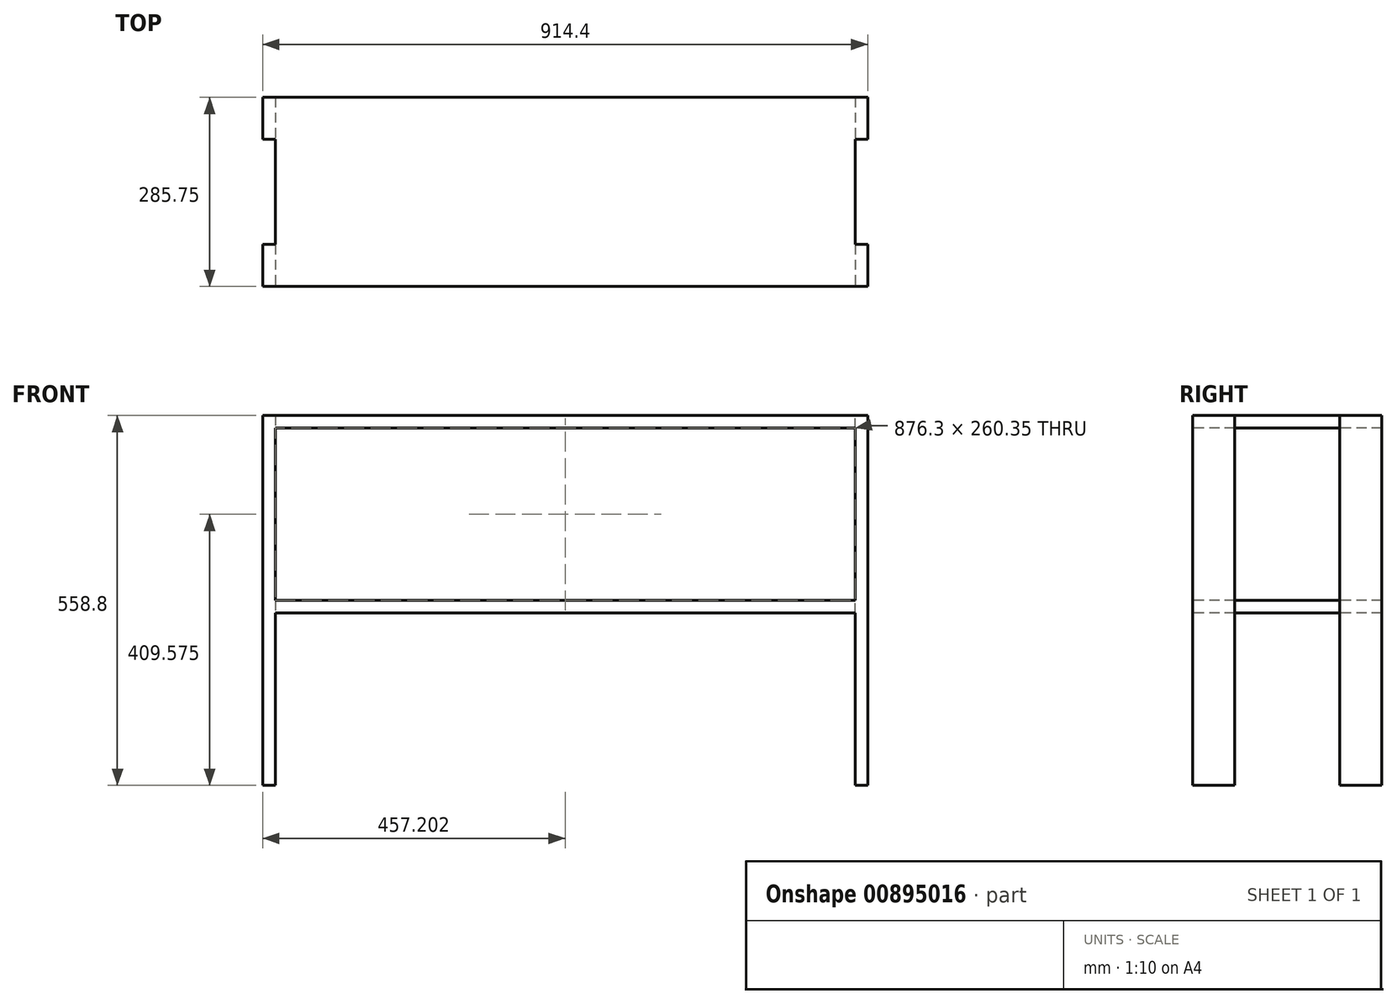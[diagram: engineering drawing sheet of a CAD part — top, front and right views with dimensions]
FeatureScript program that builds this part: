
annotation { "Feature Type Name" : "Feature", "Feature Type Description" : "" }
export const myFeature = defineFeature(function(context is Context, id is Id, definition is map)
    precondition{}
    {
        {
            var Q0;
            Q0=qCreatedBy(makeId("Front.planeOp"),FACE);
            var sketch = newSketch(context, id + "F0", { "sketchPlane" : qUnion([Q0])});
            skLineSegment(sketch, "E0.bottom", {"start": v(-1001.93, 558.8) * mm, "end": v(-87.53, 558.8) * mm});
            skLineSegment(sketch, "E0.top", {"start": v(-1001.93, 0) * mm, "end": v(-87.53, 0) * mm});
            skLineSegment(sketch, "E0.left", {"start": v(-1001.93, 558.8) * mm, "end": v(-1001.93, 0) * mm});
            skLineSegment(sketch, "E0.right", {"start": v(-87.53, 558.8) * mm, "end": v(-87.53, 0) * mm});
            skSolve(sketch);
        }
        {
            var Q0;
            Q0=makeQuery(id+"F0.imprint","IMPRINT",FACE,{"disambiguationData":[TD([[makeQuery(id+"F0.imprint","IMPRINT",EDGE,{"derivedFrom":sQuery(id+"F0.wireOp",EDGE,"E0.bottom")}),-1.0]])]});
            extrude(context, id + "F1", {"entities" : qUnion([Q0]), "depth" : 285.75 * mm, "offsetDistance" : 25.4 * mm});
        }
        {
            var Q0;
            Q0=makeQuery(id+"F1.opExtrude","CAP_FACE",FACE,{"disambiguationData":[OSD([sQuery(id+"F0.wireOp",EDGE,"E0.bottom"),sQuery(id+"F0.wireOp",EDGE,"E0.top"),sQuery(id+"F0.wireOp",EDGE,"E0.left"),sQuery(id+"F0.wireOp",EDGE,"E0.right")])],"isStart":false});
            var sketch = newSketch(context, id + "F2", { "sketchPlane" : qUnion([Q0])});
            skLineSegment(sketch, "E1.bottom", {"start": v(-982.88, 0) * mm, "end": v(-106.58, 0) * mm});
            skLineSegment(sketch, "E1.top", {"start": v(-982.88, 260.35) * mm, "end": v(-106.58, 260.35) * mm});
            skLineSegment(sketch, "E1.left", {"start": v(-982.88, 0) * mm, "end": v(-982.88, 260.35) * mm});
            skLineSegment(sketch, "E1.right", {"start": v(-106.58, 0) * mm, "end": v(-106.58, 260.35) * mm});
            skLineSegment(sketch, "E2.bottom", {"start": v(-982.88, 279.4) * mm, "end": v(-106.58, 279.4) * mm});
            skLineSegment(sketch, "E2.top", {"start": v(-982.88, 539.75) * mm, "end": v(-106.58, 539.75) * mm});
            skLineSegment(sketch, "E2.left", {"start": v(-982.88, 279.4) * mm, "end": v(-982.88, 539.75) * mm});
            skLineSegment(sketch, "E2.right", {"start": v(-106.58, 279.4) * mm, "end": v(-106.58, 539.75) * mm});
            skSolve(sketch);
        }
        {
            var Q0;
            Q0=makeQuery(id+"F2.imprint","IMPRINT",FACE,{"disambiguationData":[TD([[makeQuery(id+"F2.imprint","IMPRINT",EDGE,{"derivedFrom":sQuery(id+"F2.wireOp",EDGE,"E1.bottom")}),1.0]])]});
            var Q1;
            Q1=makeQuery(id+"F2.imprint","IMPRINT",FACE,{"disambiguationData":[TD([[makeQuery(id+"F2.imprint","IMPRINT",EDGE,{"derivedFrom":sQuery(id+"F2.wireOp",EDGE,"E2.bottom")}),1.0]])]});
            extrude(context, id + "F3", {"entities" : qUnion([Q0, Q1]), "operationType" : NewBodyOperationType.REMOVE, "endBound" : BoundingType.THROUGH_ALL, "oppositeDirection" : true, "depth" : 25.4 * mm, "offsetDistance" : 25.4 * mm});
        }
        {
            var Q0;
            Q0=makeQuery(id+"F1.opExtrude","SWEPT_FACE",FACE,{"disambiguationData":[OSD([sQuery(id+"F0.wireOp",EDGE,"E0.right")])]});
            var sketch = newSketch(context, id + "F4", { "sketchPlane" : qUnion([Q0])});
            skLineSegment(sketch, "E3.bottom", {"start": v(-222.25, 558.8) * mm, "end": v(-63.5, 558.8) * mm});
            skLineSegment(sketch, "E3.top", {"start": v(-222.25, 0) * mm, "end": v(-63.5, 0) * mm});
            skLineSegment(sketch, "E3.left", {"start": v(-222.25, 558.8) * mm, "end": v(-222.25, 0) * mm});
            skLineSegment(sketch, "E3.right", {"start": v(-63.5, 558.8) * mm, "end": v(-63.5, 0) * mm});
            skSolve(sketch);
        }
        {
            var Q0;
            Q0 = qSketchRegion(id + "F4", true);
            var Q1;
            Q1=makeQuery(id+"F3.boolean.opBoolean","COPY",FACE,{"derivedFrom":makeQuery(id+"F3.opExtrude","SWEPT_FACE",FACE,{"disambiguationData":[OSD([sQuery(id+"F2.wireOp",EDGE,"E2.right")])]})});
            extrude(context, id + "F5", {"entities" : qUnion([Q0]), "operationType" : NewBodyOperationType.REMOVE, "endBound" : BoundingType.UP_TO_SURFACE, "oppositeDirection" : true, "depth" : 25.4 * mm, "endBoundEntityFace" : qUnion([Q1]), "offsetDistance" : 25.4 * mm});
        }
        {
            var Q0;
            Q0=makeQuery(id+"F1.opExtrude","SWEPT_FACE",FACE,{"disambiguationData":[OSD([sQuery(id+"F0.wireOp",EDGE,"E0.left")])]});
            var sketch = newSketch(context, id + "F6", { "sketchPlane" : qUnion([Q0])});
            skLineSegment(sketch, "E4.bottom", {"start": v(63.5, 558.8) * mm, "end": v(222.25, 558.8) * mm});
            skLineSegment(sketch, "E4.top", {"start": v(63.5, 0) * mm, "end": v(222.25, 0) * mm});
            skLineSegment(sketch, "E4.left", {"start": v(63.5, 558.8) * mm, "end": v(63.5, 0) * mm});
            skLineSegment(sketch, "E4.right", {"start": v(222.25, 558.8) * mm, "end": v(222.25, 0) * mm});
            skSolve(sketch);
        }
        {
            var Q0;
            Q0 = qSketchRegion(id + "F6", true);
            var Q1;
            Q1=makeQuery(id+"F3.boolean.opBoolean","COPY",FACE,{"derivedFrom":makeQuery(id+"F3.opExtrude","SWEPT_FACE",FACE,{"disambiguationData":[OSD([sQuery(id+"F2.wireOp",EDGE,"E2.left")])]})});
            extrude(context, id + "F7", {"entities" : qUnion([Q0]), "operationType" : NewBodyOperationType.REMOVE, "endBound" : BoundingType.UP_TO_SURFACE, "oppositeDirection" : true, "depth" : 25.4 * mm, "endBoundEntityFace" : qUnion([Q1]), "offsetDistance" : 25.4 * mm});
        }
    });
